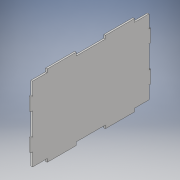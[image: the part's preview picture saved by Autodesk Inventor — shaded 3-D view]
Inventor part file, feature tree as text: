
AUTODESK INVENTOR PART (.ipt)
format: ipt  version: 2017 (Build 210142000, 142)  size: 158,720 bytes
history: native  units: in
note: dims shown in document units (in); Inventor stores cm internally (conversion verified against a paired STEP export)
features: extrude x3, sketch x3, plane x2, mirror x2, projected_geometry x1
ambient origin geometry x8: Origin, YZ Plane, XZ Plane, XY Plane, X Axis, Y Axis, Z Axis, Center Point
bodies: Solid1 (feature_tree)
feature tree (11):
  extrude  "Extrusion1"  Depth=72.0in
  extrude  "Extrusion2"  Depth=9.0in
  extrude  "Extrusion3"  Depth=2.0in TaperAngle=0.0deg
  plane  "Work Plane1"
  mirror  "Mirror1"
  plane  "Work Plane2"
  mirror  "Mirror2"
  sketch  "Sketch1"  dims[d0=46.0in d1=72.0in]
  sketch  "Sketch2"  dims[d2=1.0in d3=0.0in d4=9.0in]
  sketch  "Sketch3"  dims[d5=18.0in d6=2.0in d7=0.0in d8=8.0in d9=8.0in d10=1.0in d11=0.0in d12=8.0in d13=14.0in]
  projected_geometry  "Projected Loop1"
